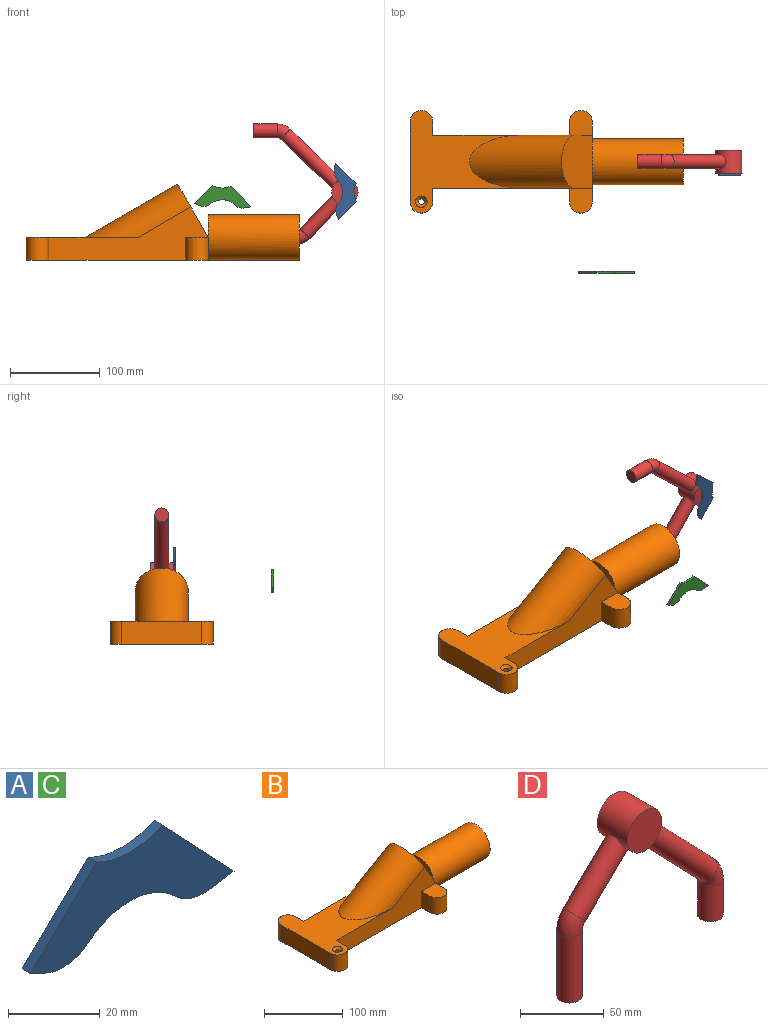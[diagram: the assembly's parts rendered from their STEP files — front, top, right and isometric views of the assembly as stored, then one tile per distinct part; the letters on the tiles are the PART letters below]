
ASSEMBLY  parts=4 mates=2
PART A: 10 faces, bbox 62.7x2.5x24.8 mm
  f0: plane 4.68x2.54mm, normal (-0.43,0,-0.9), area 13.1mm2, adj f1,f7,f8,f9
  f1: cylinder r=12.7mm len=13.46mm, axis (0,1,0), area 36.3mm2, adj f0,f2,f8,f9
  f2: cylinder r=19.87mm len=26.48mm, axis (0,1,0), area 73.7mm2, adj f1,f3,f8,f9
  f3: cylinder r=12.7mm len=10.83mm, axis (0,1,0), area 29.9mm2, adj f2,f4,f8,f9
  f4: plane 7.26x2.54mm, normal (0.15,0,-0.99), area 18.7mm2, adj f3,f5,f8,f9
  f5: plane 23.27x22.08mm, normal (0.73,0,0.69), area 81.5mm2, adj f4,f6,f8,f9
  f6: cylinder r=23.13mm len=20.28mm, axis (0,1,0), area 53.3mm2, adj f5,f7,f8,f9
  f7: plane 20.34x19.51mm, normal (-0.69,0,0.72), area 71.6mm2, adj f0,f6,f8,f9
  f8: plane 62.71x24.8mm, normal (0,-1,0), area 787.2mm2, adj f0,f1,f2,f3,f4,f5,f6,f7
  f9: plane 62.71x24.8mm, normal (0,1,0), area 787.2mm2, adj f0,f1,f2,f3,f4,f5,f6,f7
PART B: 24 faces, bbox 304.8x114.3x85 mm
  f0: plane 44.45x25.4mm, normal (1,0,0), area 622.3mm2, adj f3,f6,f16,f18,f20
  f1: plane 44.45x25.4mm, normal (1,0,0), area 622.3mm2, adj f7,f15,f16,f18,f20
  f2: plane 125.27x114.3mm, normal (0,0,1), area 5796.7mm2, adj f4,f9,f10,f11,f12,f13,f14,f17
  f3: plane 27.64x25.4mm, normal (0,0,1), area 632.7mm2, adj f0,f4,f5,f6
  f4: plane 177.8x59.14mm, normal (0,-1,0), area 5185.8mm2, adj f2,f3,f5,f14,f16,f17,f18
  f5: plane 25.4x14.94mm, normal (-1,0,0), area 379.4mm2, adj f3,f4,f6,f16
  f6: cylinder r=12.7mm len=25.4mm, axis (0,0,-1), area 1013.4mm2, adj f0,f3,f5,f16
  f7: cylinder r=12.7mm len=25.4mm, axis (0,0,-1), area 1013.4mm2, adj f1,f8,f15,f16
  f8: plane 25.4x14.94mm, normal (-1,0,0), area 379.4mm2, adj f7,f9,f15,f16
  f9: plane 177.8x59.14mm, normal (0,1,0), area 5185.8mm2, adj f2,f8,f10,f15,f16,f17,f18
  f10: plane 25.4x14.94mm, normal (1,0,0), area 379.4mm2, adj f2,f9,f11,f16
  f11: cylinder r=12.7mm len=25.4mm, axis (0,0,-1), area 1013.4mm2, adj f2,f10,f12,f16
  f12: plane 88.9x25.4mm, normal (-1,0,0), area 2258.1mm2, adj f2,f11,f13,f16
  f13: cylinder r=12.7mm len=25.4mm, axis (0,0,-1), area 1013.4mm2, adj f2,f12,f14,f16
  f14: plane 25.4x14.94mm, normal (1,0,0), area 379.4mm2, adj f2,f4,f13,f16
  f15: plane 27.64x25.4mm, normal (0,0,1), area 632.7mm2, adj f1,f7,f8,f9
  f16: plane 203.2x114.3mm, normal (0,0,-1), area 14494mm2, adj f0,f1,f4,f5,f6,f7,f8,f9
  f17: cylinder r=29.51mm len=117.63mm, axis (0.87,0,0.5), area 9275.5mm2, adj f2,f4,f9,f18
  f18: plane 59.31x59.03mm, normal (0.87,0,0.5), area 3668.4mm2, adj f0,f1,f4,f9,f17,f19
  f19: plane 50.8x25.4mm, normal (-1,0,0), area 1013.4mm2, adj f18,f20
  f20: cylinder r=25.4mm len=101.6mm, axis (-1,0,0), area 16214.6mm2, adj f0,f1,f19,f21
  f21: plane 50.8x50.8mm, normal (1,0,0), area 2026.8mm2, adj f20
  f22: cylinder r=3.17mm len=22.23mm, axis (0,0,1), area 443.4mm2, adj f16,f23
  f23: cone r=3.17mm half-angle=45deg, axis (0,0,1), area 134.4mm2, adj f2,f22
PART C: same geometry as A
PART D: 11 faces, bbox 137.3x25.4x116 mm
  f0: cylinder r=14.61mm len=29.21mm, axis (0,1,0), area 1950.7mm2, adj f1,f2,f6,f7
  f1: plane 29.21x29.21mm, normal (0,-1,0), area 670.1mm2, adj f0
  f2: plane 29.21x29.21mm, normal (0,1,0), area 670.1mm2, adj f0
  f3: plane 15.26x15.26mm, normal (0,0,-1), area 182.9mm2, adj f4
  f4: cylinder r=7.63mm len=26mm, axis (0,0,1), area 1246.7mm2, adj f3,f5
  f5: torus R=13.1mm, axis (0,-1,0), area 481.3mm2, adj f4,f6
  f6: cylinder r=7.63mm len=68.39mm, axis (-0.69,0,0.72), area 3783.6mm2, adj f0,f5
  f7: cylinder r=7.63mm len=48.07mm, axis (-0.72,0,-0.69), area 2430.9mm2, adj f0,f9
  f8: plane 15.26x15.26mm, normal (0,0,-1), area 182.9mm2, adj f10
  f9: torus R=13.1mm, axis (0,-1,0), area 504.9mm2, adj f7,f10
  f10: cylinder r=7.63mm len=47.69mm, axis (0,0,-1), area 2286.8mm2, adj f8,f9
PLACE A rot(axis=(-0.71,0,-0.71),180deg) t=(100.45,67.61,80.36)mm
PLACE B t=(-186.79,111.1,4.53)mm
PLACE C t=(-69.67,-41.73,107.86)mm
PLACE D rot(axis=(-0.71,0,-0.71),180deg) t=(67.01,81.58,80.48)mm
MATE fastened D.f10 <-> B.f20  axis (-1,0,0) through (-34.39,81.58,29.93)mm
MATE fastened D.f0 <-> A.f8  axis (0,-1,0) through (67.01,68.88,80.48)mm
